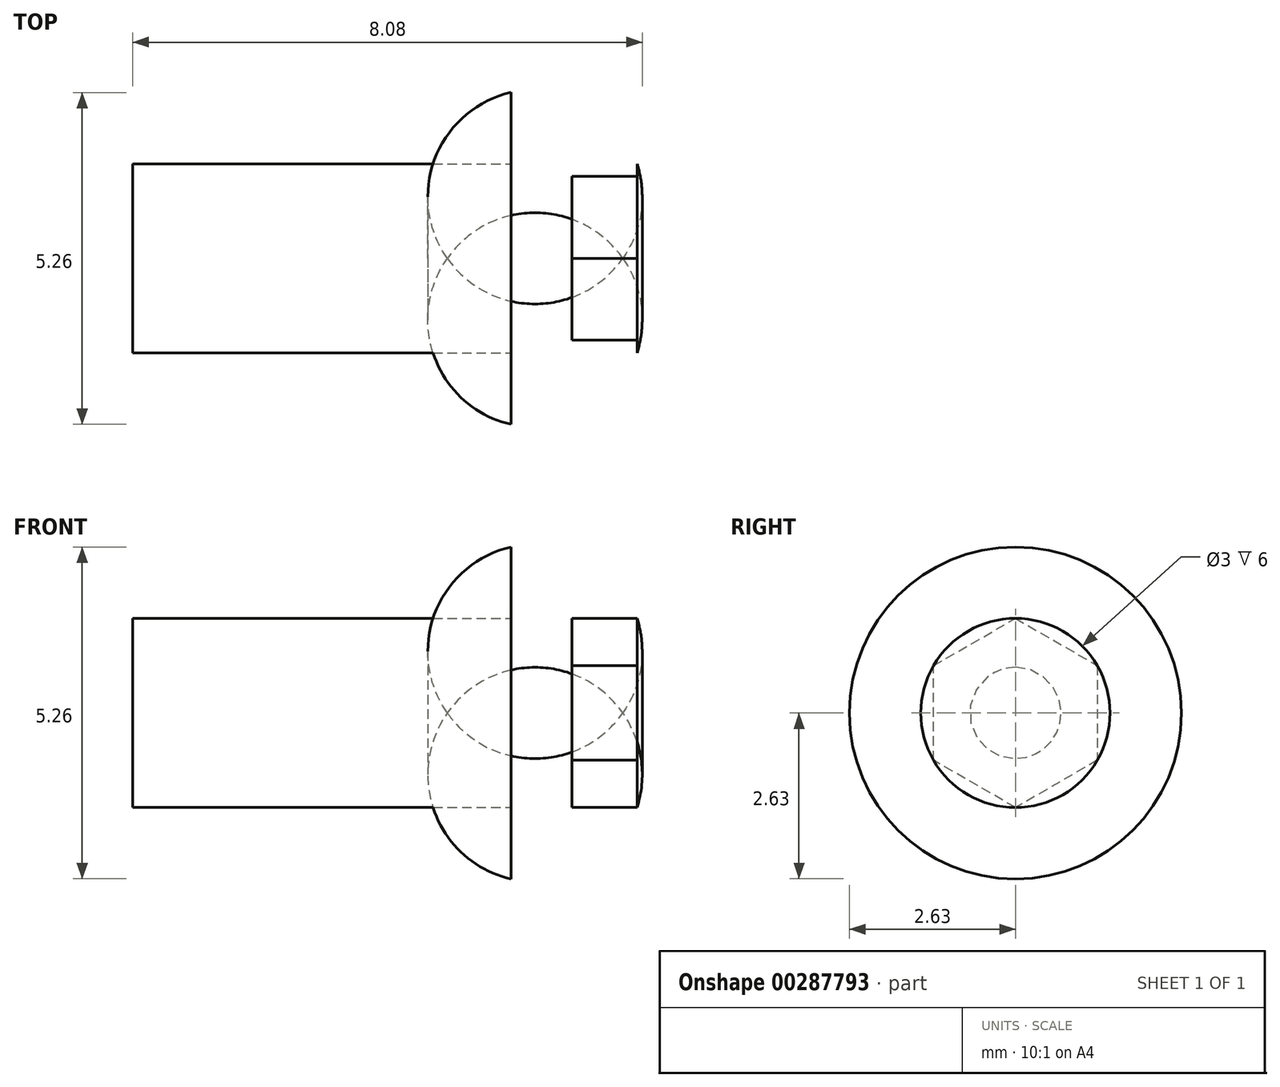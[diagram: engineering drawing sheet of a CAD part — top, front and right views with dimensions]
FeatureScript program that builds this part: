
annotation { "Feature Type Name" : "Feature", "Feature Type Description" : "" }
export const myFeature = defineFeature(function(context is Context, id is Id, definition is map)
    precondition{}
    {
        {
            var Q0;
            Q0=qCreatedBy(makeId("Front.planeOp"),FACE);
            var sketch = newSketch(context, id + "F0", { "sketchPlane" : qUnion([Q0])});
            skLineSegment(sketch, "E0", {"start": v(5.32, 0) * mm, "end": v(5.32, 1.5) * mm});
            skLineSegment(sketch, "E1", {"start": v(5.32, 0) * mm, "end": v(-2.68, 0) * mm});
            skLineSegment(sketch, "E2", {"start": v(-2.68, 0) * mm, "end": v(-2.68, 1.5) * mm});
            skLineSegment(sketch, "E3", {"start": v(-2.68, 1.5) * mm, "end": v(3.32, 1.5) * mm});
            skLineSegment(sketch, "E4", {"start": v(3.32, 1.5) * mm, "end": v(3.32, 2.63) * mm});
            skArc(sketch, "E5", {"start": v(5.32, 1.5) * mm, "mid": v(4.54, 2.46) * mm, "end": v(3.32, 2.63) * mm});
            skSolve(sketch);
        }
        {
            var Q0;
            Q0 = qSketchRegion(id + "F0", true);
            var Q1;
            Q1=sQuery(id+"F0.wireOp",EDGE,"E1");
            revolve(context, id + "F1", {"entities" : qUnion([Q0]), "axis" : qUnion([Q1]), "revolveType" : RevolveType.FULL});
        }
        {
            var Q0;
            Q0=makeQuery(id+"F1.opRevolve","SWEPT_FACE",FACE,{"disambiguationData":[OSD([sQuery(id+"F0.wireOp",EDGE,"E0")])]});
            var sketch = newSketch(context, id + "F2", { "sketchPlane" : qUnion([Q0])});
            skPoint(sketch, "E6", {"position": v(0, 0) * mm});
            skLineSegment(sketch, "E7.0", {"start": v(1.3, -0.75) * mm, "end": v(0, -1.5) * mm});
            skLineSegment(sketch, "E7.1", {"start": v(0, -1.5) * mm, "end": v(-1.3, -0.75) * mm});
            skLineSegment(sketch, "E7.2", {"start": v(-1.3, -0.75) * mm, "end": v(-1.3, 0.75) * mm});
            skLineSegment(sketch, "E7.3", {"start": v(-1.3, 0.75) * mm, "end": v(0, 1.5) * mm});
            skLineSegment(sketch, "E7.4", {"start": v(0, 1.5) * mm, "end": v(1.3, 0.75) * mm});
            skLineSegment(sketch, "E7.5", {"start": v(1.3, 0.75) * mm, "end": v(1.3, -0.75) * mm});
            skSolve(sketch);
        }
        {
            var Q0;
            Q0 = qSketchRegion(id + "F2", true);
            extrude(context, id + "F3", {"entities" : qUnion([Q0]), "operationType" : NewBodyOperationType.REMOVE, "oppositeDirection" : true, "depth" : 1.03 * mm});
        }
    });
